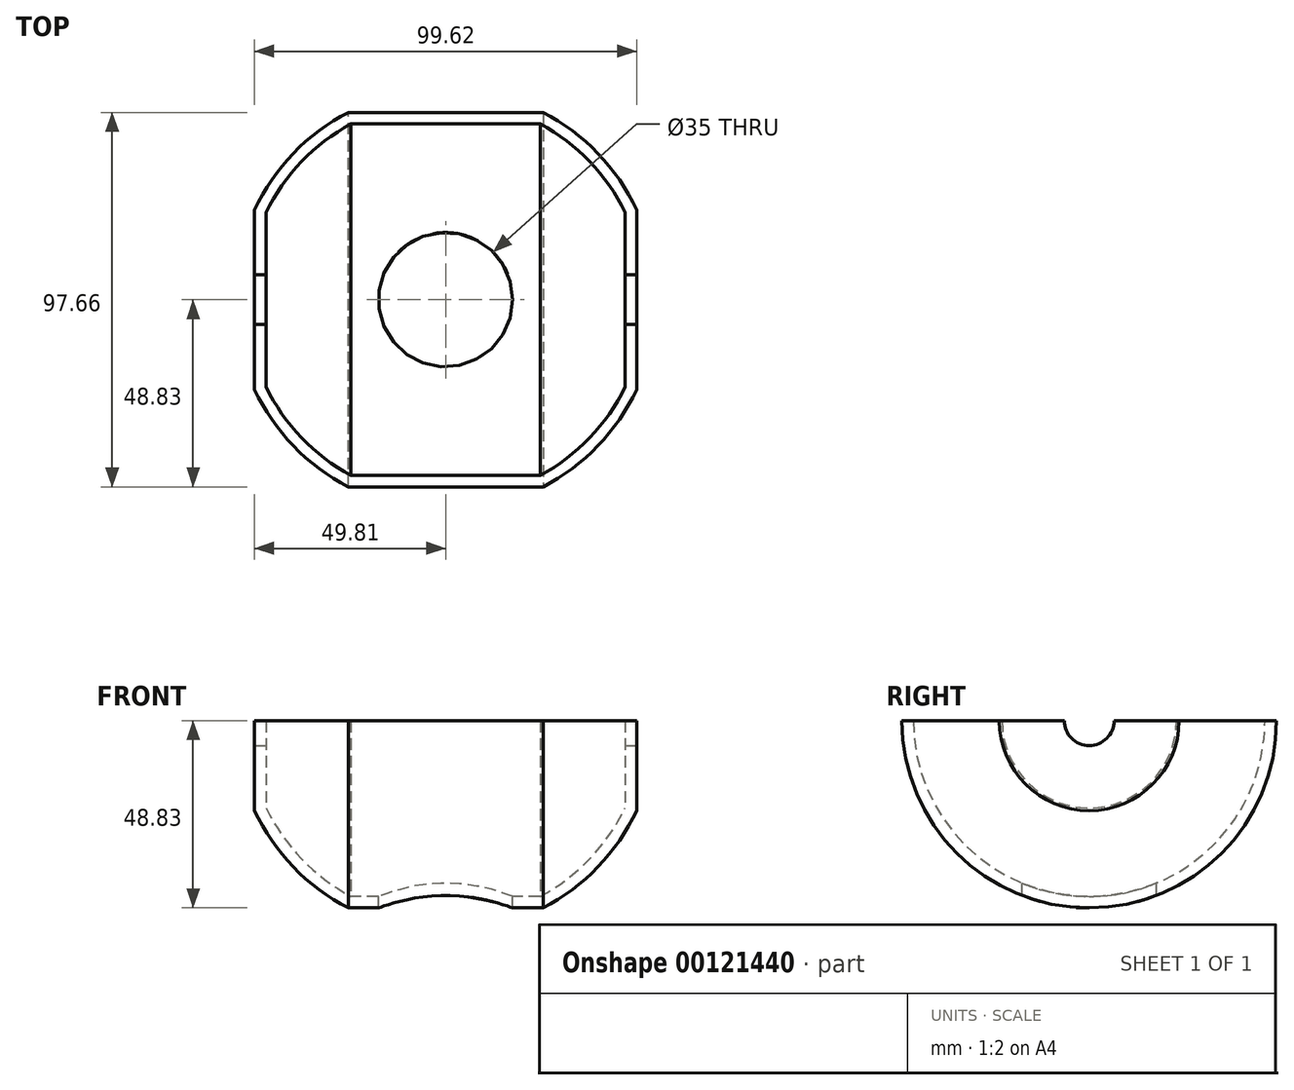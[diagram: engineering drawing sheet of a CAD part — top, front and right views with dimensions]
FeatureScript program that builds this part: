
annotation { "Feature Type Name" : "Feature", "Feature Type Description" : "" }
export const myFeature = defineFeature(function(context is Context, id is Id, definition is map)
    precondition{}
    {
        {
            var Q0;
            Q0=qCreatedBy(makeId("Top.planeOp"),FACE);
            var sketch = newSketch(context, id + "F0", { "sketchPlane" : qUnion([Q0])});
            skArc(sketch, "E0", {"start": v(0, -55.05) * mm, "mid": v(55.05, 0) * mm, "end": v(0, 55.05) * mm});
            skLineSegment(sketch, "E1", {"start": v(0, 0) * mm, "end": v(0, 55.05) * mm});
            skLineSegment(sketch, "E2", {"start": v(0, 0) * mm, "end": v(0, -55.05) * mm});
            skSolve(sketch);
        }
        {
            var Q0;
            Q0=qSketchRegion(id+"F0",true);
            var Q1;
            Q1=sQuery(id+"F0.wireOp",EDGE,"E1");
            revolve(context, id + "F1", {"entities" : qUnion([Q0]), "axis" : qUnion([Q1]), "revolveType" : RevolveType.FULL});
        }
        {
            var Q0;
            Q0=qCreatedBy(makeId("Top.planeOp"),FACE);
            var sketch = newSketch(context, id + "F2", { "sketchPlane" : qUnion([Q0])});
            skLineSegment(sketch, "E3", {"start": v(-49.81, 26.1) * mm, "end": v(-49.81, -26.1) * mm});
            skLineSegment(sketch, "E4", {"start": v(-49.81, 26.1) * mm, "end": v(-57.5, 26.1) * mm});
            skLineSegment(sketch, "E5", {"start": v(-57.5, 26.1) * mm, "end": v(-57.5, -26.1) * mm});
            skLineSegment(sketch, "E6", {"start": v(-57.5, -26.1) * mm, "end": v(-49.81, -26.1) * mm});
            skLineSegment(sketch, "E7.MirrorCS", {"start": v(49.81, 26.1) * mm, "end": v(49.81, -26.1) * mm});
            skLineSegment(sketch, "E8.MirrorCS", {"start": v(49.81, 26.1) * mm, "end": v(57.5, 26.1) * mm});
            skLineSegment(sketch, "E9.MirrorCS", {"start": v(57.5, 26.1) * mm, "end": v(57.5, -26.1) * mm});
            skLineSegment(sketch, "E10.MirrorCS", {"start": v(57.5, -26.1) * mm, "end": v(49.81, -26.1) * mm});
            skPoint(sketch, "E11.end.orphan", {"position": v(-49.81, 0) * mm});
            skSolve(sketch);
        }
        {
            var Q0;
            Q0=qSketchRegion(id+"F2",true);
            extrude(context, id + "F3", {"entities" : qUnion([Q0]), "operationType" : NewBodyOperationType.REMOVE, "endBound" : BoundingType.SYMMETRIC, "oppositeDirection" : true, "depth" : 50 * mm});
        }
        {
            var Q0;
            Q0=qCreatedBy(makeId("Right.planeOp"),FACE);
            var sketch = newSketch(context, id + "F4", { "sketchPlane" : qUnion([Q0])});
            skLineSegment(sketch, "E12", {"start": v(-5.9, 34.63) * mm, "end": v(42.8, 34.63) * mm});
            skLineSegment(sketch, "E13", {"start": v(-5.9, 34.63) * mm, "end": v(-32.1, 14.27) * mm});
            skLineSegment(sketch, "E14", {"start": v(-32.1, 14.27) * mm, "end": v(-53.17, 14.27) * mm});
            skArc(sketch, "E15", {"start": v(42.8, 34.63) * mm, "mid": v(-11.42, 53.85) * mm, "end": v(-53.17, 14.27) * mm});
            skPoint(sketch, "E16.orphan", {"position": v(-42.8, 34.63) * mm});
            skSolve(sketch);
        }
        {
            var Q0;
            Q0=qSketchRegion(id+"F4",true);
            extrude(context, id + "F5", {"entities" : qUnion([Q0]), "operationType" : NewBodyOperationType.REMOVE, "endBound" : BoundingType.SYMMETRIC, "oppositeDirection" : true, "depth" : 100 * mm});
        }
        {
            var Q0;
            Q0=qCreatedBy(makeId("Right.planeOp"),FACE);
            var sketch = newSketch(context, id + "F6", { "sketchPlane" : qUnion([Q0])});
            skCircle(sketch, "E17", {"center": v(0, 0) * mm, "radius": 6.5 * mm});
            skSolve(sketch);
        }
        {
            var Q0;
            Q0=qSketchRegion(id+"F6",true);
            extrude(context, id + "F7", {"entities" : qUnion([Q0]), "operationType" : NewBodyOperationType.REMOVE, "endBound" : BoundingType.SYMMETRIC, "oppositeDirection" : true, "depth" : 100 * mm});
        }
        {
            var Q0;
            Q0=qCreatedBy(makeId("Right.planeOp"),FACE);
            var sketch = newSketch(context, id + "F8", { "sketchPlane" : qUnion([Q0])});
            skCircle(sketch, "E18", {"center": v(0, 0) * mm, "radius": 64.9 * mm});
            skCircle(sketch, "E19", {"center": v(0, 0) * mm, "radius": 48.83 * mm});
            skSolve(sketch);
        }
        {
            var Q0;
            Q0=qSketchRegion(id+"F8",true);
            extrude(context, id + "F9", {"entities" : qUnion([Q0]), "operationType" : NewBodyOperationType.REMOVE, "endBound" : BoundingType.SYMMETRIC, "depth" : 100 * mm});
        }
        {
            var Q0;
            Q0=qCreatedBy(makeId("Right.planeOp"),FACE);
            var sketch = newSketch(context, id + "F10", { "sketchPlane" : qUnion([Q0])});
            skLineSegment(sketch, "E20", {"start": v(-46.4, 28.07) * mm, "end": v(-5.9, 34.63) * mm});
            skLineSegment(sketch, "E21", {"start": v(-46.4, 28.07) * mm, "end": v(-48.15, 8.16) * mm});
            skLineSegment(sketch, "E22", {"start": v(-5.9, 34.63) * mm, "end": v(-34.33, 9.36) * mm});
            skLineSegment(sketch, "E23", {"start": v(-34.33, 9.36) * mm, "end": v(-48.15, 8.16) * mm});
            skSolve(sketch);
        }
        {
            var Q0;
            Q0=qSketchRegion(id+"F10",true);
            extrude(context, id + "F11", {"entities" : qUnion([Q0]), "operationType" : NewBodyOperationType.ADD, "endBound" : BoundingType.SYMMETRIC, "depth" : 30.5 * mm});
        }
        {
            var Q0;
            Q0=qCreatedBy(makeId("Right.planeOp"),FACE);
            var sketch = newSketch(context, id + "F12", { "sketchPlane" : qUnion([Q0])});
            skLineSegment(sketch, "E24", {"start": v(-64.02, 0) * mm, "end": v(62.32, 0) * mm});
            skLineSegment(sketch, "E25", {"start": v(-64.02, 0) * mm, "end": v(-64.02, 48.44) * mm});
            skLineSegment(sketch, "E26", {"start": v(-64.02, 48.44) * mm, "end": v(62.32, 48.44) * mm});
            skLineSegment(sketch, "E27", {"start": v(62.32, 48.44) * mm, "end": v(62.32, 0) * mm});
            skSolve(sketch);
        }
        {
            var Q0;
            Q0=qSketchRegion(id+"F12",true);
            extrude(context, id + "F13", {"entities" : qUnion([Q0]), "operationType" : NewBodyOperationType.REMOVE, "endBound" : BoundingType.SYMMETRIC, "oppositeDirection" : true, "depth" : 100 * mm});
        }
        {
            var Q0;
            Q0=makeQuery(id+"F13.boolean.opBoolean","COPY",FACE,{"disambiguationData":[OD(0.0)],"derivedFrom":makeQuery(id+"F13.opExtrude","SWEPT_FACE",FACE,{"disambiguationData":[OSD([sQuery(id+"F12.wireOp",EDGE,"E24")])]})});
            var Q1;
            Q1=makeQuery(id+"F13.boolean.opBoolean","COPY",FACE,{"disambiguationData":[OD(1.0)],"derivedFrom":makeQuery(id+"F13.opExtrude","SWEPT_FACE",FACE,{"disambiguationData":[OSD([sQuery(id+"F12.wireOp",EDGE,"E24")])]})});
            var Q2;
            Q2=makeQuery(id+"F7.boolean.opBoolean","COPY",FACE,{"derivedFrom":makeQuery(id+"F7.opExtrude","SWEPT_FACE",FACE,{"disambiguationData":[OSD([sQuery(id+"F6.wireOp",EDGE,"E17")])]})});
            shell(context, id + "F14", {"entities" : qUnion([Q0, Q1, Q2]), "thickness" : 3 * mm});
        }
        {
            var Q0;
            Q0=qCreatedBy(makeId("Top.planeOp"),FACE);
            var sketch = newSketch(context, id + "F15", { "sketchPlane" : qUnion([Q0])});
            skCircle(sketch, "E28", {"center": v(0, 0) * mm, "radius": 17.5 * mm});
            skSolve(sketch);
        }
        {
            var Q0;
            Q0 = qSketchRegion(id + "F15", true);
            extrude(context, id + "F16", {"entities" : qUnion([Q0]), "operationType" : NewBodyOperationType.REMOVE, "oppositeDirection" : true, "depth" : 66.2 * mm});
        }
    });
